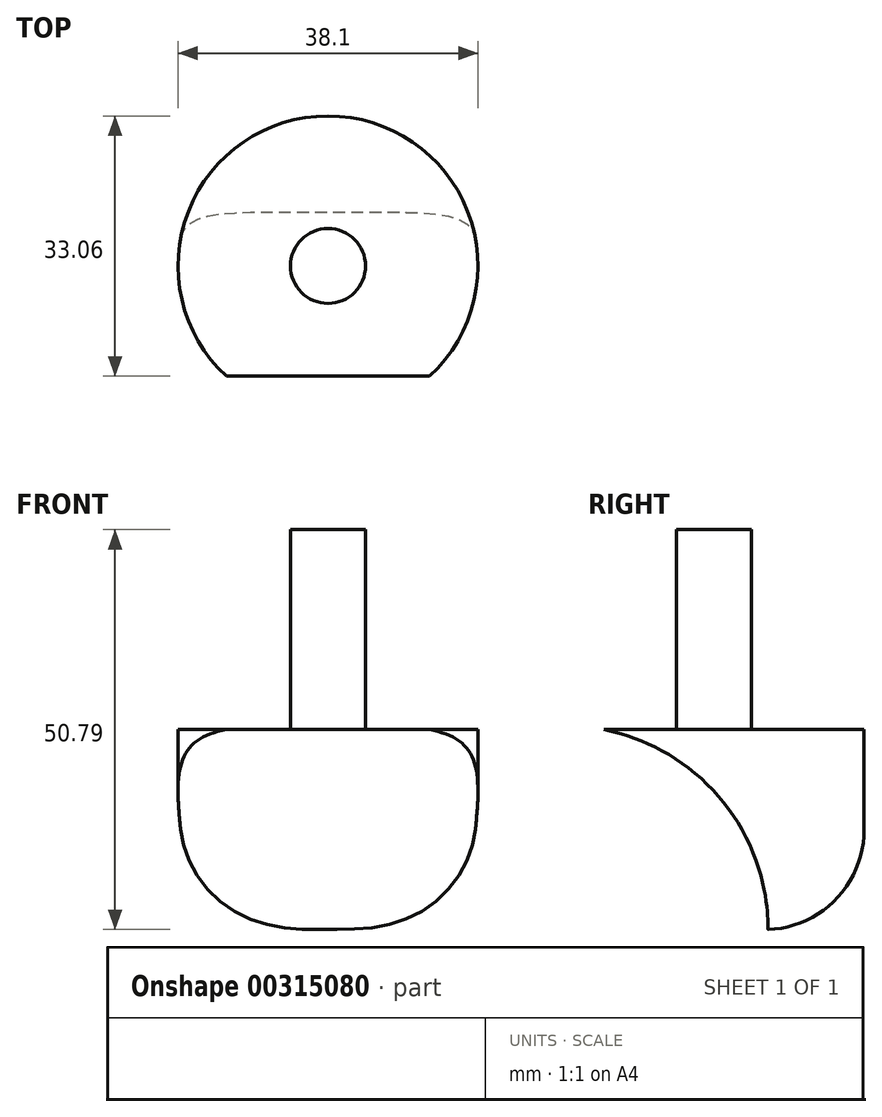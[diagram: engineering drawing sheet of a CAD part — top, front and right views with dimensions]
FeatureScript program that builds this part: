
annotation { "Feature Type Name" : "Feature", "Feature Type Description" : "" }
export const myFeature = defineFeature(function(context is Context, id is Id, definition is map)
    precondition{}
    {
        {
            var Q0;
            Q0=qCreatedBy(makeId("Top.planeOp"),FACE);
            var sketch = newSketch(context, id + "F0", { "sketchPlane" : qUnion([Q0])});
            skCircle(sketch, "E0", {"center": v(0, 0) * mm, "radius": 19.05 * mm});
            skCircle(sketch, "E1", {"center": v(0, 0) * mm, "radius": 4.76 * mm});
            skSolve(sketch);
        }
        {
            var Q0;
            Q0=makeQuery(id+"F0.imprint","IMPRINT",FACE,{"disambiguationData":[TD([[makeQuery(id+"F0.imprint","IMPRINT",EDGE,{"derivedFrom":sQuery(id+"F0.wireOp",EDGE,"E0")}),1.0]])]});
            extrude(context, id + "F1", {"entities" : qUnion([Q0]), "depth" : 25.4 * mm});
        }
        {
            var Q0;
            Q0=makeQuery(id+"F0.imprint","IMPRINT",FACE,{"disambiguationData":[TD([[makeQuery(id+"F0.imprint","IMPRINT",EDGE,{"derivedFrom":sQuery(id+"F0.wireOp",EDGE,"E1")}),1.0]])]});
            extrude(context, id + "F2", {"entities" : qUnion([Q0]), "operationType" : NewBodyOperationType.ADD, "depth" : 50.8 * mm});
        }
        {
            var Q0;
            Q0=qCreatedBy(makeId("Front.planeOp"),FACE);
            var sketch = newSketch(context, id + "F3", { "sketchPlane" : qUnion([Q0])});
            skCircle(sketch, "E2", {"center": v(19.05, 0) * mm, "radius": 25.9 * mm});
            skSolve(sketch);
        }
        {
            var Q0;
            Q0=makeQuery(id+"F1.opExtrude","CAP_EDGE",EDGE,{"disambiguationData":[OSD([sQuery(id+"F0.wireOp",EDGE,"E0")])],"isStart":true});
            fillet(context, id + "F4", {"entities" : qUnion([Q0]), "radius" : 12.7 * mm, "tangentPropagation" : true, "allowEdgeOverflow" : false});
        }
        {
            var Q0;
            Q0=makeQuery(id+"F3.imprint","IMPRINT",FACE,{"disambiguationData":[TD([[makeQuery(id+"F3.imprint","IMPRINT",EDGE,{"derivedFrom":sQuery(id+"F3.wireOp",EDGE,"E2")}),1.0]])]});
            extrude(context, id + "F5", {"entities" : qUnion([Q0]), "operationType" : NewBodyOperationType.REMOVE, "endBound" : BoundingType.THROUGH_ALL, "oppositeDirection" : true, "depth" : 25.4 * mm});
        }
        {
            var Q0;
            Q0 = qSketchRegion(id + "F3", true);
            extrude(context, id + "F6", {"entities" : qUnion([Q0]), "operationType" : NewBodyOperationType.REMOVE, "depth" : 25.4 * mm});
        }
        {
            var Q0;
            Q0=makeQuery(id+"F1.opExtrude","SWEPT_BODY",BODY,{"disambiguationData":[OSD([sQuery(id+"F0.wireOp",EDGE,"E0"),sQuery(id+"F0.wireOp",EDGE,"E1")])]});
            var Q1;
            Q1=makeQuery(id+"F2.opExtrude","SWEPT_FACE",FACE,{"disambiguationData":[OSD([sQuery(id+"F0.wireOp",EDGE,"E1")])]});
            transform(context, id + "F7", {"entities" : qUnion([Q0]), "transformType" : TransformType.ROTATION, "transformAxis" : qUnion([Q1]), "angle" : 90 * degree, "makeCopy" : false});
        }
    });
